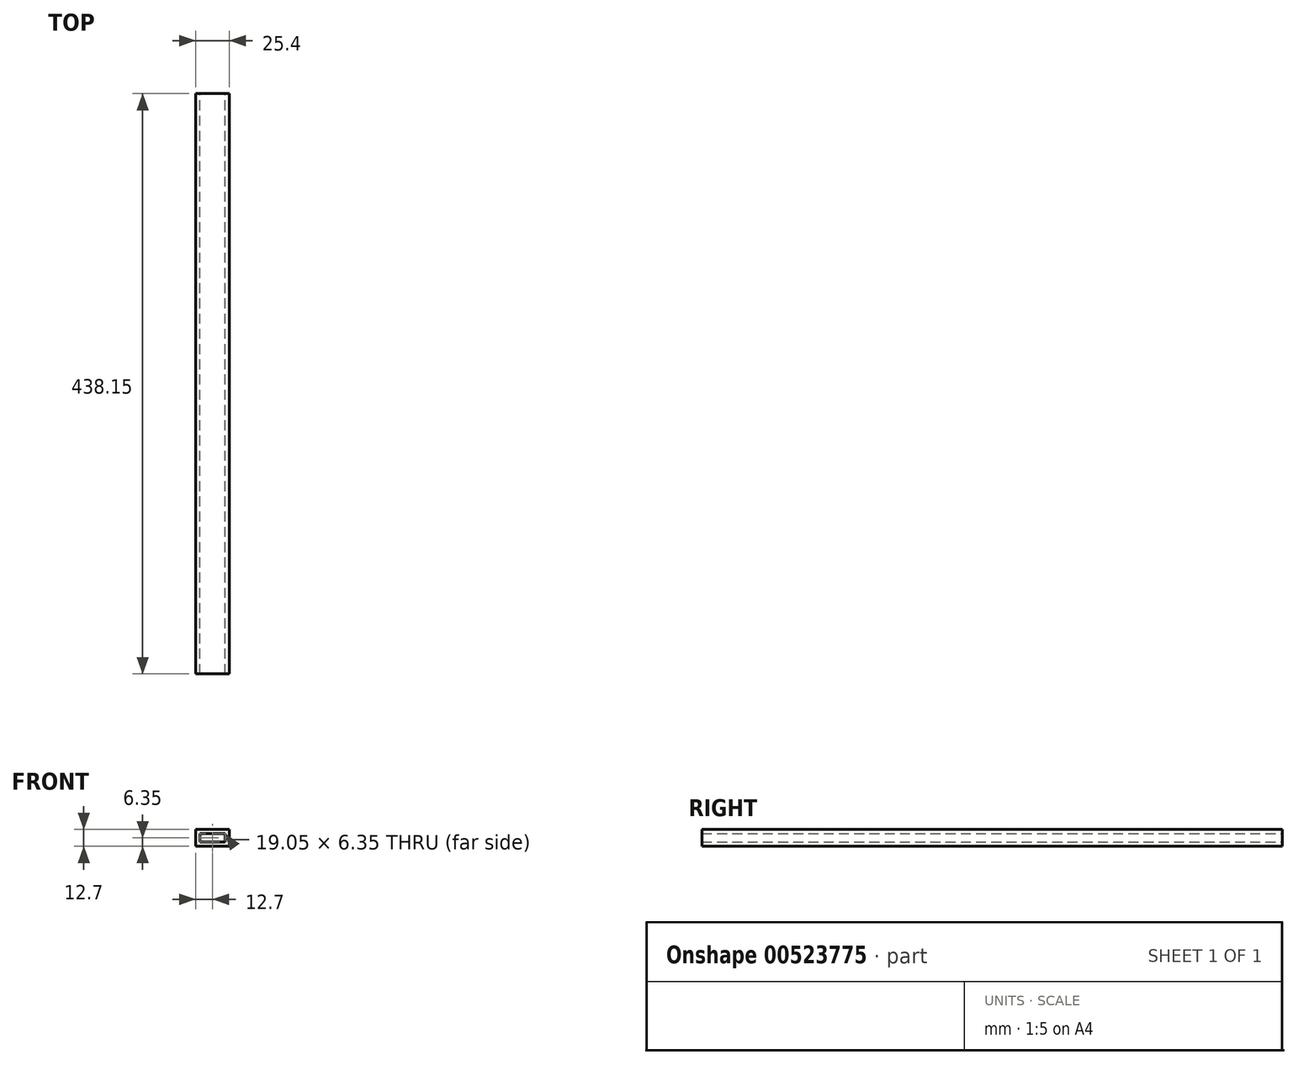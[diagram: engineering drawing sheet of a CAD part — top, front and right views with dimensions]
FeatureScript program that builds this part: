
annotation { "Feature Type Name" : "Feature", "Feature Type Description" : "" }
export const myFeature = defineFeature(function(context is Context, id is Id, definition is map)
    precondition{}
    {
        {
            var Q0;
            Q0=qCreatedBy(makeId("Front.planeOp"),FACE);
            var sketch = newSketch(context, id + "F0", { "sketchPlane" : qUnion([Q0])});
            skLineSegment(sketch, "E0", {"start": v(0, 0) * mm, "end": v(-25.4, 0) * mm});
            skLineSegment(sketch, "E1", {"start": v(-25.4, 0) * mm, "end": v(-25.4, 12.7) * mm});
            skLineSegment(sketch, "E2", {"start": v(-25.4, 12.7) * mm, "end": v(0, 12.7) * mm});
            skLineSegment(sketch, "E3", {"start": v(0, 12.7) * mm, "end": v(0, 0) * mm});
            skLineSegment(sketch, "E4", {"start": v(-25.4, 12.7) * mm, "end": v(-25.4, 9.52) * mm});
            skLineSegment(sketch, "E5", {"start": v(-22.23, 9.52) * mm, "end": v(-3.18, 9.52) * mm});
            skLineSegment(sketch, "E6", {"start": v(-3.18, 9.52) * mm, "end": v(-3.18, 3.18) * mm});
            skLineSegment(sketch, "E7", {"start": v(-3.18, 3.18) * mm, "end": v(-22.23, 3.18) * mm});
            skLineSegment(sketch, "E8", {"start": v(-22.23, 3.18) * mm, "end": v(-22.23, 9.52) * mm});
            skSolve(sketch);
        }
        {
            var Q0;
            Q0=makeQuery(id+"F0.imprint","IMPRINT",FACE,{"disambiguationData":[TD([[makeQuery(id+"F0.imprint","IMPRINT",EDGE,{"derivedFrom":sQuery(id+"F0.wireOp",EDGE,"E0")}),-1.0]])]});
            extrude(context, id + "F1", {"entities" : qUnion([Q0]), "depth" : 265.43 * mm, "offsetDistance" : 25.4 * mm});
        }
        {
            var Q0;
            Q0=makeQuery(id+"F1.opExtrude","CAP_FACE",FACE,{"disambiguationData":[OSD([sQuery(id+"F0.wireOp",EDGE,"E0"),sQuery(id+"F0.wireOp",EDGE,"E1"),sQuery(id+"F0.wireOp",EDGE,"E2"),sQuery(id+"F0.wireOp",EDGE,"E3"),sQuery(id+"F0.wireOp",EDGE,"E4"),sQuery(id+"F0.wireOp",EDGE,"E5"),sQuery(id+"F0.wireOp",EDGE,"E6"),sQuery(id+"F0.wireOp",EDGE,"E7"),sQuery(id+"F0.wireOp",EDGE,"E8")])],"isStart":false});
            var sketch = newSketch(context, id + "F2", { "sketchPlane" : qUnion([Q0])});
            skLineSegment(sketch, "E9.bottom", {"start": v(-22.23, 9.52) * mm, "end": v(-3.18, 9.52) * mm});
            skLineSegment(sketch, "E9.top", {"start": v(-22.23, 3.18) * mm, "end": v(-3.18, 3.18) * mm});
            skLineSegment(sketch, "E9.left", {"start": v(-22.23, 9.52) * mm, "end": v(-22.23, 3.18) * mm});
            skLineSegment(sketch, "E9.right", {"start": v(-3.18, 9.52) * mm, "end": v(-3.18, 3.18) * mm});
            skLineSegment(sketch, "E10.bottom", {"start": v(-25.4, 12.7) * mm, "end": v(0, 12.7) * mm});
            skLineSegment(sketch, "E10.top", {"start": v(-25.4, 0) * mm, "end": v(0, 0) * mm});
            skLineSegment(sketch, "E10.left", {"start": v(-25.4, 12.7) * mm, "end": v(-25.4, 0) * mm});
            skLineSegment(sketch, "E10.right", {"start": v(0, 12.7) * mm, "end": v(0, 0) * mm});
            skSolve(sketch);
        }
        {
            var Q0;
            Q0=makeQuery(id+"F2.imprint","IMPRINT",FACE,{"disambiguationData":[TD([[makeQuery(id+"F2.imprint","IMPRINT",EDGE,{"derivedFrom":sQuery(id+"F2.wireOp",EDGE,"E9.bottom")}),1.0]])]});
            extrude(context, id + "F3", {"entities" : qUnion([Q0]), "operationType" : NewBodyOperationType.ADD, "depth" : 86.36 * mm, "offsetDistance" : 25.4 * mm});
        }
        {
            var Q0;
            Q0=makeQuery(id+"F1.opExtrude","CAP_FACE",FACE,{"disambiguationData":[OSD([sQuery(id+"F0.wireOp",EDGE,"E0"),sQuery(id+"F0.wireOp",EDGE,"E1"),sQuery(id+"F0.wireOp",EDGE,"E2"),sQuery(id+"F0.wireOp",EDGE,"E3"),sQuery(id+"F0.wireOp",EDGE,"E4"),sQuery(id+"F0.wireOp",EDGE,"E5"),sQuery(id+"F0.wireOp",EDGE,"E6"),sQuery(id+"F0.wireOp",EDGE,"E7"),sQuery(id+"F0.wireOp",EDGE,"E8")])],"isStart":true});
            extrude(context, id + "F4", {"entities" : qUnion([Q0]), "operationType" : NewBodyOperationType.ADD, "depth" : 86.36 * mm, "offsetDistance" : 25.4 * mm});
        }
    });
